# Revit family: Envirocoustic Wood Wool panel
name_source: partatom
category: Generic Models
units: mm (PartAtom-declared; Revit-internal decimal feet)

## family parameters
Always vertical = No
Can host rebar = No
Cut with Voids When Loaded = No
Maintain Annotation Orientation = No
Part Type = Normal
Room Calculation Point = No
Round Connector Dimension = Use Diameter
Shared = No
Work Plane-Based = Yes

## types (24) — shared parameters
Default Elevation = 4' - 0"
Manufacturer = Acoustical Surfaces, Inc.
Material = Envirocoustic Wood Wool
T = 0' - 1"
URL = https://www.acousticalsurfaces.com
Width = 2' - 0"
‍      0. Thickness 1" = Yes
‍      1. Thickness 1-3/8" = No
‍      2. Thickness 2" = No
zero-valued in all types: Thickness Options

## per-type parameters (varying)
| type | A | Backfill | Edge Option | Finish | Length | ‍     1. Beveled | ‍     2. Square |
| Square 2x8 Custom Painted | 0' - 0" | No | 2 | Custom Painted | 8' - 0" | No | Yes |
| Square 2x4 Custom Painted | 0' - 0" | No | 2 | Custom Painted | 4' - 0" | No | Yes |
| Square 2x8 Primed White | 0' - 0" | No | 2 | Primed White | 8' - 0" | No | Yes |
| Square 2x4 Primed White | 0' - 0" | No | 2 | Primed White | 4' - 0" | No | Yes |
| Square 2x8 Primed Clear | 0' - 0" | No | 2 | Primed Clear | 8' - 0" | No | Yes |
| Square 2x4 Primed Clear | 0' - 0" | No | 2 | Primed Clear | 4' - 0" | No | Yes |
| Square 2x8 Custom Painted With Backfill | 0' - 1" | Yes | 2 | Custom Painted | 8' - 0" | No | Yes |
| Square 2x4 Custom Painted With Backfill | 0' - 1" | Yes | 2 | Custom Painted | 4' - 0" | No | Yes |
| Square 2x8 Primed White With Backfill | 0' - 1" | Yes | 2 | Primed White | 8' - 0" | No | Yes |
| Square 2x4 Primed White With Backfill | 0' - 1" | Yes | 2 | Primed White | 4' - 0" | No | Yes |
| Square 2x8 Primed Clear With Backfill | 0' - 1" | Yes | 2 | Primed Clear | 8' - 0" | No | Yes |
| Square 2x4 Primed Clear With Backfill | 0' - 1" | Yes | 2 | Primed Clear | 4' - 0" | No | Yes |
| Beveled 2x8 Custom Painted | 0' - 0" | No | 1 | Custom Painted | 8' - 0" | Yes | No |
| Beveled 2x4 Custom Painted | 0' - 0" | No | 1 | Custom Painted | 4' - 0" | Yes | No |
| Beveled 2x8 Primed White | 0' - 0" | No | 1 | Primed White | 8' - 0" | Yes | No |
| Beveled 2x4 Primed White | 0' - 0" | No | 1 | Primed White | 4' - 0" | Yes | No |
| Beveled 2x8 Primed Clear | 0' - 0" | No | 1 | Primed Clear | 8' - 0" | Yes | No |
| Beveled 2x4 Primed Clear | 0' - 0" | No | 1 | Primed Clear | 4' - 0" | Yes | No |
| Beveled 2x8 Custom Painted With Backfill | 0' - 1" | Yes | 1 | Custom Painted | 8' - 0" | Yes | No |
| Beveled 2x4 Custom Painted With Backfill | 0' - 1" | Yes | 1 | Custom Painted | 4' - 0" | Yes | No |
| Beveled 2x8 Primed White With Backfill | 0' - 1" | Yes | 1 | Primed White | 8' - 0" | Yes | No |
| Beveled 2x4 Primed White With Backfill | 0' - 1" | Yes | 1 | Primed White | 4' - 0" | Yes | No |
| Beveled 2x8 Primed Clear With Backfill | 0' - 1" | Yes | 1 | Primed Clear | 8' - 0" | Yes | No |
| Beveled 2x4 Primed Clear With Backfill | 0' - 1" | Yes | 1 | Primed Clear | 4' - 0" | Yes | No |

## geometry (parser evidence)
native form markers: Sweep x9
no freeform markers — native parametric forms only
